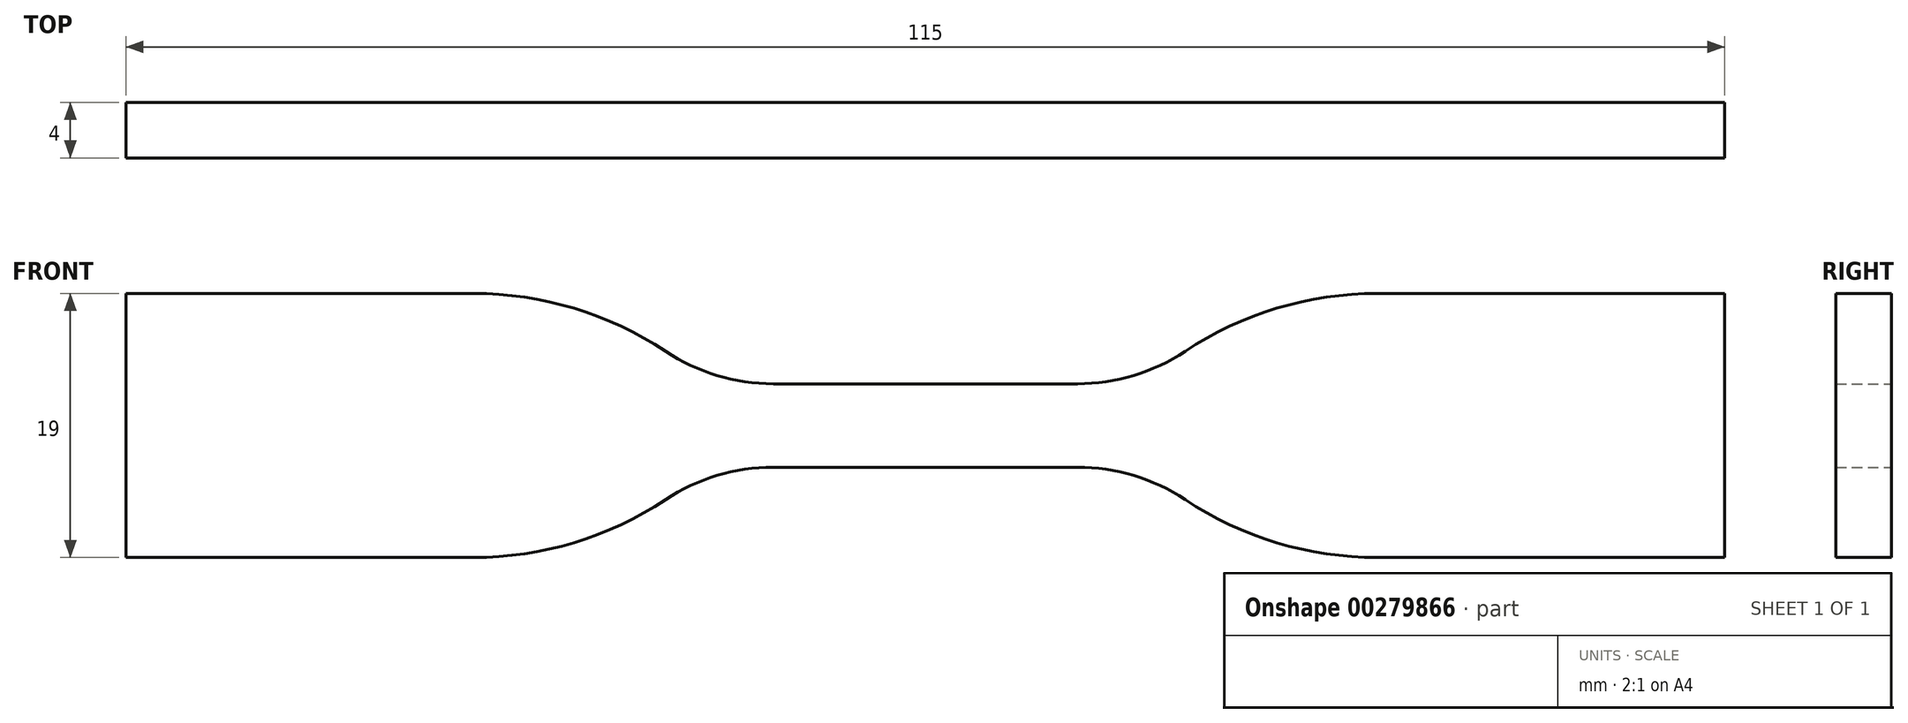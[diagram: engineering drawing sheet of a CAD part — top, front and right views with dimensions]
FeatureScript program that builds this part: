
annotation { "Feature Type Name" : "Feature", "Feature Type Description" : "" }
export const myFeature = defineFeature(function(context is Context, id is Id, definition is map)
    precondition{}
    {
        {
            var Q0;
            Q0=qCreatedBy(makeId("Front.planeOp"),FACE);
            var sketch = newSketch(context, id + "F0", { "sketchPlane" : qUnion([Q0])});
            skLineSegment(sketch, "E0", {"start": v(0, 3) * mm, "end": v(10.94, 3) * mm});
            skLineSegment(sketch, "E1", {"start": v(32.5, 9.5) * mm, "end": v(57.5, 9.5) * mm});
            skArc(sketch, "E2.MirrorCS", {"start": v(18.68, -5.33) * mm, "mid": v(25.28, -8.44) * mm, "end": v(32.5, -9.5) * mm});
            skLineSegment(sketch, "E3.MirrorCS", {"start": v(32.5, -9.5) * mm, "end": v(57.5, -9.5) * mm});
            skLineSegment(sketch, "E4.MirrorCS", {"start": v(0, -3) * mm, "end": v(10.94, -3) * mm});
            skLineSegment(sketch, "E5.MirrorCS", {"start": v(0, -3) * mm, "end": v(-10.94, -3) * mm});
            skLineSegment(sketch, "E6.MirrorCS", {"start": v(0, 3) * mm, "end": v(-10.94, 3) * mm});
            skLineSegment(sketch, "E7.MirrorCS", {"start": v(-32.5, -9.5) * mm, "end": v(-57.5, -9.5) * mm});
            skLineSegment(sketch, "E8.MirrorCS", {"start": v(-32.5, 9.5) * mm, "end": v(-57.5, 9.5) * mm});
            skLineSegment(sketch, "E9", {"start": v(-57.5, 9.5) * mm, "end": v(-57.5, -9.5) * mm});
            skLineSegment(sketch, "E10", {"start": v(57.5, 9.5) * mm, "end": v(57.5, -9.5) * mm});
            skArc(sketch, "E11", {"start": v(-18.68, 5.33) * mm, "mid": v(-25.28, 8.44) * mm, "end": v(-32.5, 9.5) * mm});
            skPoint(sketch, "E12.visualSharp", {"position": v(-15.68, 3) * mm});
            skArc(sketch, "E12.filletArc", {"start": v(-18.68, 5.33) * mm, "mid": v(-14.98, 3.6) * mm, "end": v(-10.94, 3) * mm});
            skArc(sketch, "E13", {"start": v(-32.5, -9.5) * mm, "mid": v(-25.28, -8.44) * mm, "end": v(-18.68, -5.33) * mm});
            skPoint(sketch, "E14.visualSharp", {"position": v(-15.68, -3) * mm});
            skArc(sketch, "E14.filletArc", {"start": v(-10.94, -3) * mm, "mid": v(-14.98, -3.6) * mm, "end": v(-18.68, -5.33) * mm});
            skArc(sketch, "E15", {"start": v(32.5, 9.5) * mm, "mid": v(25.28, 8.44) * mm, "end": v(18.68, 5.33) * mm});
            skPoint(sketch, "E16.visualSharp", {"position": v(15.68, 3) * mm});
            skArc(sketch, "E16.filletArc", {"start": v(10.94, 3) * mm, "mid": v(14.98, 3.6) * mm, "end": v(18.68, 5.33) * mm});
            skPoint(sketch, "E17.visualSharp", {"position": v(15.68, -3) * mm});
            skArc(sketch, "E17.filletArc", {"start": v(18.68, -5.33) * mm, "mid": v(14.98, -3.6) * mm, "end": v(10.94, -3) * mm});
            skSolve(sketch);
        }
        {
            var Q0;
            Q0=makeQuery(id+"F0.imprint","IMPRINT",FACE,{"disambiguationData":[TD([[makeQuery(id+"F0.imprint","IMPRINT",EDGE,{"derivedFrom":sQuery(id+"F0.wireOp",EDGE,"E0")}),-1.0]])]});
            extrude(context, id + "F1", {"entities" : qUnion([Q0]), "endBound" : BoundingType.SYMMETRIC, "depth" : 4 * mm});
        }
    });
